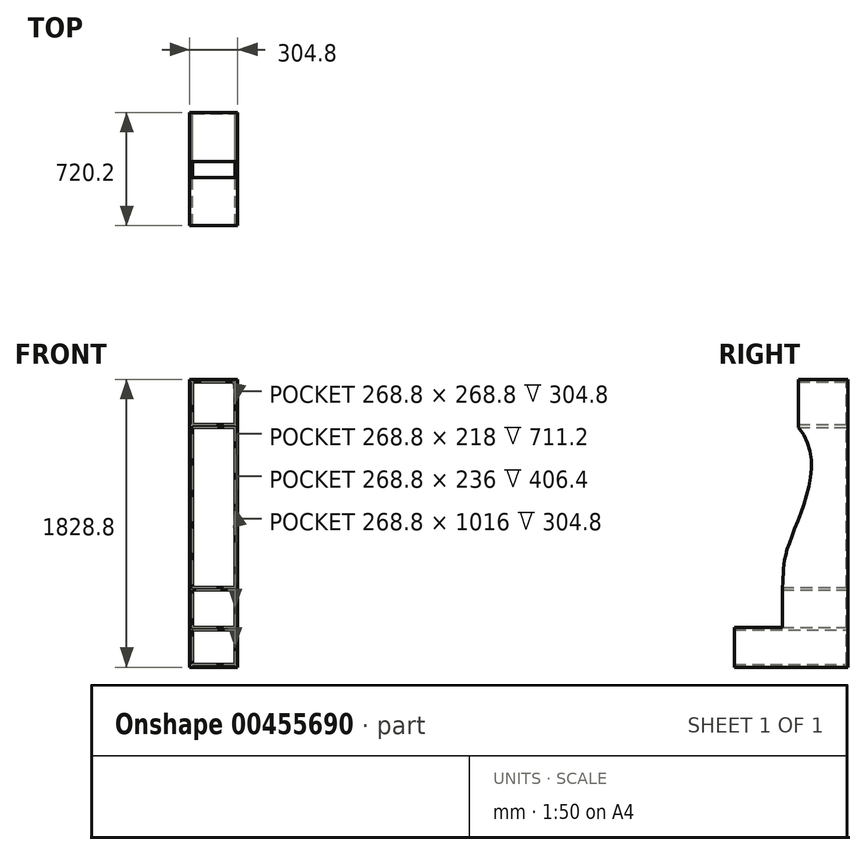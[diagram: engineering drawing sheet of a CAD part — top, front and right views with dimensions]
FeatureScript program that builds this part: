
annotation { "Feature Type Name" : "Feature", "Feature Type Description" : "" }
export const myFeature = defineFeature(function(context is Context, id is Id, definition is map)
    precondition{}
    {
        {
            var Q0;
            Q0=qCreatedBy(makeId("Front.planeOp"),FACE);
            var sketch = newSketch(context, id + "F0", { "sketchPlane" : qUnion([Q0])});
            skLineSegment(sketch, "E0.bottom", {"start": v(0, 0) * mm, "end": v(304.8, 0) * mm});
            skLineSegment(sketch, "E0.top", {"start": v(0, 1828.8) * mm, "end": v(304.8, 1828.8) * mm});
            skLineSegment(sketch, "E0.left", {"start": v(0, 0) * mm, "end": v(0, 1828.8) * mm});
            skLineSegment(sketch, "E0.right", {"start": v(304.8, 0) * mm, "end": v(304.8, 1828.8) * mm});
            skLineSegment(sketch, "E1", {"start": v(0, 254) * mm, "end": v(304.8, 254) * mm});
            skLineSegment(sketch, "E2", {"start": v(0, 508) * mm, "end": v(304.8, 508) * mm});
            skLineSegment(sketch, "E3", {"start": v(18, 1524) * mm, "end": v(286.8, 1524) * mm});
            skPoint(sketch, "E3.endSnap0", {"position": v(304.8, 914.4) * mm});
            skLineSegment(sketch, "E4.0", {"start": v(18, 236) * mm, "end": v(286.8, 236) * mm});
            skLineSegment(sketch, "E5.0", {"start": v(286.8, 18) * mm, "end": v(286.8, 236) * mm});
            skLineSegment(sketch, "E6.0", {"start": v(18, 18) * mm, "end": v(18, 236) * mm});
            skLineSegment(sketch, "E7.0", {"start": v(18, 490) * mm, "end": v(286.8, 490) * mm});
            skLineSegment(sketch, "E8.0", {"start": v(18, 18) * mm, "end": v(286.8, 18) * mm});
            skLineSegment(sketch, "E9.0", {"start": v(18, 1810.8) * mm, "end": v(286.8, 1810.8) * mm});
            skLineSegment(sketch, "E10.0", {"start": v(18, 1542) * mm, "end": v(286.8, 1542) * mm});
            skLineSegment(sketch, "E11.trimOffspring", {"start": v(286.8, 1542) * mm, "end": v(286.8, 1810.8) * mm});
            skPoint(sketch, "E12.orphan", {"position": v(304.8, 1524) * mm});
            skLineSegment(sketch, "E13.trimOffspring", {"start": v(18, 1542) * mm, "end": v(18, 1810.8) * mm});
            skLineSegment(sketch, "E14.trimOffspring", {"start": v(18, 508) * mm, "end": v(18, 1524) * mm});
            skLineSegment(sketch, "E15.trimOffspring", {"start": v(286.8, 508) * mm, "end": v(286.8, 1524) * mm});
            skLineSegment(sketch, "E16.trimOffspring", {"start": v(18, 254) * mm, "end": v(18, 490) * mm});
            skLineSegment(sketch, "E17.trimOffspring", {"start": v(286.8, 254) * mm, "end": v(286.8, 490) * mm});
            skSolve(sketch);
        }
        {
            var Q0;
            Q0=makeQuery(id+"F0.imprint","IMPRINT",FACE,{"disambiguationData":[TD([[makeQuery(id+"F0.imprint","IMPRINT",EDGE,{"derivedFrom":sQuery(id+"F0.wireOp",EDGE,"E7.0")}),1.0]])]});
            var sketch = newSketch(context, id + "F1", { "sketchPlane" : qUnion([Q0])});
            skLineSegment(sketch, "E18.0", {"start": v(18, 254) * mm, "end": v(18, 490) * mm});
            skLineSegment(sketch, "E18.1", {"start": v(18, 490) * mm, "end": v(286.8, 490) * mm});
            skLineSegment(sketch, "E18.2", {"start": v(286.8, 254) * mm, "end": v(286.8, 490) * mm});
            skLineSegment(sketch, "E18.3", {"start": v(0, 508) * mm, "end": v(304.8, 508) * mm});
            skLineSegment(sketch, "E18.4", {"start": v(0, 254) * mm, "end": v(0, 508) * mm});
            skLineSegment(sketch, "E18.5", {"start": v(304.8, 254) * mm, "end": v(304.8, 508) * mm});
            skPoint(sketch, "E19.orphan", {"position": v(0, 1828.8) * mm});
            skPoint(sketch, "E20.orphan", {"position": v(304.8, 1828.8) * mm});
            skLineSegment(sketch, "E21", {"start": v(0, 254) * mm, "end": v(18, 254) * mm});
            skLineSegment(sketch, "E22", {"start": v(286.8, 254) * mm, "end": v(304.8, 254) * mm});
            skPoint(sketch, "E23.orphan", {"position": v(304.8, 0) * mm});
            skPoint(sketch, "E24.orphan", {"position": v(0, 0) * mm});
            skSolve(sketch);
        }
        {
            var Q0;
            {var subQ4=sQuery(id+"F0.wireOp",EDGE,"E0.top");Q0=makeQuery(id+"F0.imprint","IMPRINT",FACE,{"disambiguationData":[TD([[makeQuery(id+"F0.imprint","IMPRINT",EDGE,{"derivedFrom":subQ4}),-1.0]])]});}
            var sketch = newSketch(context, id + "F2", { "sketchPlane" : qUnion([Q0])});
            skLineSegment(sketch, "E25.0", {"start": v(18, 1810.8) * mm, "end": v(286.8, 1810.8) * mm});
            skLineSegment(sketch, "E25.1", {"start": v(18, 1542) * mm, "end": v(18, 1810.8) * mm});
            skLineSegment(sketch, "E25.2", {"start": v(18, 1542) * mm, "end": v(286.8, 1542) * mm});
            skLineSegment(sketch, "E25.3", {"start": v(286.8, 1542) * mm, "end": v(286.8, 1810.8) * mm});
            skLineSegment(sketch, "E25.4", {"start": v(304.8, 1524) * mm, "end": v(304.8, 1828.8) * mm});
            skLineSegment(sketch, "E25.5", {"start": v(0, 1828.8) * mm, "end": v(304.8, 1828.8) * mm});
            skLineSegment(sketch, "E25.6", {"start": v(0, 1524) * mm, "end": v(0, 1828.8) * mm});
            skLineSegment(sketch, "E25.7", {"start": v(18, 1524) * mm, "end": v(286.8, 1524) * mm});
            skPoint(sketch, "E25.8", {"position": v(152.4, 1542) * mm});
            skLineSegment(sketch, "E26", {"start": v(18, 1524) * mm, "end": v(0, 1524) * mm});
            skLineSegment(sketch, "E27", {"start": v(286.8, 1524) * mm, "end": v(304.8, 1524) * mm});
            skPoint(sketch, "E28.orphan", {"position": v(304.8, 0) * mm});
            skPoint(sketch, "E29.orphan", {"position": v(0, 0) * mm});
            skSolve(sketch);
        }
        {
            var Q0;
            {var subQ4=sQuery(id+"F0.wireOp",EDGE,"E0.top");Q0=makeQuery(id+"F0.imprint","IMPRINT",FACE,{"disambiguationData":[TD([[makeQuery(id+"F0.imprint","IMPRINT",EDGE,{"derivedFrom":subQ4}),-1.0]])]});}
            var sketch = newSketch(context, id + "F3", { "sketchPlane" : qUnion([Q0])});
            skLineSegment(sketch, "E30.0", {"start": v(18, 508) * mm, "end": v(18, 1524) * mm});
            skLineSegment(sketch, "E30.1", {"start": v(0, 508) * mm, "end": v(0, 1524) * mm});
            skLineSegment(sketch, "E30.2", {"start": v(286.8, 508) * mm, "end": v(286.8, 1524) * mm});
            skLineSegment(sketch, "E30.3", {"start": v(304.8, 508) * mm, "end": v(304.8, 1524) * mm});
            skLineSegment(sketch, "E31", {"start": v(286.8, 508) * mm, "end": v(304.8, 508) * mm});
            skLineSegment(sketch, "E32", {"start": v(18, 508) * mm, "end": v(0, 508) * mm});
            skLineSegment(sketch, "E33", {"start": v(18, 1524) * mm, "end": v(0, 1524) * mm});
            skLineSegment(sketch, "E34", {"start": v(286.8, 1524) * mm, "end": v(304.8, 1524) * mm});
            skPoint(sketch, "E35.orphan", {"position": v(0, 1828.8) * mm});
            skPoint(sketch, "E36.orphan", {"position": v(304.8, 1828.8) * mm});
            skPoint(sketch, "E37.orphan", {"position": v(304.8, 0) * mm});
            skPoint(sketch, "E38.orphan", {"position": v(0, 0) * mm});
            skSolve(sketch);
        }
        {
            var Q0;
            {var subQ4=sQuery(id+"F0.wireOp",EDGE,"E0.bottom");Q0=makeQuery(id+"F0.imprint","IMPRINT",FACE,{"disambiguationData":[TD([[makeQuery(id+"F0.imprint","IMPRINT",EDGE,{"derivedFrom":subQ4}),1.0]])]});}
            extrude(context, id + "F4", {"entities" : qUnion([Q0]), "depth" : 711.2 * mm});
        }
        {
            var Q0;
            Q0 = qSketchRegion(id + "F1", true);
            extrude(context, id + "F5", {"entities" : qUnion([Q0]), "operationType" : NewBodyOperationType.ADD, "depth" : 406.4 * mm});
        }
        {
            var Q0;
            Q0 = qSketchRegion(id + "F2", true);
            extrude(context, id + "F6", {"entities" : qUnion([Q0]), "depth" : 304.8 * mm});
        }
        {
            var Q0;
            Q0 = qSketchRegion(id + "F3", true);
            extrude(context, id + "F7", {"entities" : qUnion([Q0]), "operationType" : NewBodyOperationType.ADD, "depth" : 406.4 * mm});
        }
        {
            var Q0;
            Q0=makeQuery(id+"F7.boolean.opBoolean","MERGE",FACE,{"derivedFrom":[makeQuery(id+"F5.boolean.opBoolean","MERGE",FACE,{"derivedFrom":[makeQuery(id+"F4.opExtrude","SWEPT_FACE",FACE,{"disambiguationData":[OSD([sQuery(id+"F0.wireOp",EDGE,"E0.right")])]}),makeQuery(id+"F5.opExtrude","SWEPT_FACE",FACE,{"disambiguationData":[OSD([sQuery(id+"F1.wireOp",EDGE,"E18.5")])]})]}),makeQuery(id+"F6.opExtrude","SWEPT_FACE",FACE,{"disambiguationData":[OSD([sQuery(id+"F2.wireOp",EDGE,"E25.4")])]}),makeQuery(id+"F7.opExtrude","SWEPT_FACE",FACE,{"disambiguationData":[OSD([sQuery(id+"F3.wireOp",EDGE,"E30.3")])]})]});
            var sketch = newSketch(context, id + "F8", { "sketchPlane" : qUnion([Q0])});
            skPoint(sketch, "E39.0", {"position": v(-406.4, 508) * mm});
            skFitSpline(sketch, "E40", {"points": [v(-406.4, 508) * mm, v(-369.4, 767.64) * mm, v(-304.8, 1524) * mm], "startDerivative": vector(77.57, 734.22) * mm, "endDerivative": vector(-918.38, 1059.14) * mm});
            skLineSegment(sketch, "E41", {"start": v(-304.8, 1524) * mm, "end": v(-406.4, 1524) * mm});
            skLineSegment(sketch, "E42", {"start": v(-406.4, 1524) * mm, "end": v(-406.4, 508) * mm});
            skSolve(sketch);
        }
        {
            var Q0;
            Q0 = qSketchRegion(id + "F8", true);
            extrude(context, id + "F9", {"entities" : qUnion([Q0]), "operationType" : NewBodyOperationType.ADD, "depth" : 25.4 * mm});
        }
        {
            var Q0;
            Q0=makeQuery(id+"F9.opExtrude","CAP_FACE",FACE,{"disambiguationData":[OSD([sQuery(id+"F8.wireOp",EDGE,"E40"),sQuery(id+"F8.wireOp",EDGE,"E41"),sQuery(id+"F8.wireOp",EDGE,"E42")])],"isStart":false});
            extrude(context, id + "F10", {"entities" : qUnion([Q0]), "operationType" : NewBodyOperationType.REMOVE, "endBound" : BoundingType.THROUGH_ALL, "oppositeDirection" : true, "depth" : 25.4 * mm});
        }
        {
            var Q0;
            Q0=makeQuery(id+"F7.boolean.opBoolean","MERGE",FACE,{"derivedFrom":[makeQuery(id+"F5.boolean.opBoolean","MERGE",FACE,{"derivedFrom":[makeQuery(id+"F4.opExtrude","CAP_FACE",FACE,{"disambiguationData":[OSD([sQuery(id+"F0.wireOp",EDGE,"E0.bottom"),sQuery(id+"F0.wireOp",EDGE,"E0.left"),sQuery(id+"F0.wireOp",EDGE,"E0.right"),sQuery(id+"F0.wireOp",EDGE,"E1"),sQuery(id+"F0.wireOp",EDGE,"E4.0"),sQuery(id+"F0.wireOp",EDGE,"E5.0"),sQuery(id+"F0.wireOp",EDGE,"E6.0"),sQuery(id+"F0.wireOp",EDGE,"E8.0")])],"isStart":true}),makeQuery(id+"F5.opExtrude","CAP_FACE",FACE,{"disambiguationData":[OSD([sQuery(id+"F1.wireOp",EDGE,"E18.0"),sQuery(id+"F1.wireOp",EDGE,"E18.1"),sQuery(id+"F1.wireOp",EDGE,"E18.2"),sQuery(id+"F1.wireOp",EDGE,"E18.3"),sQuery(id+"F1.wireOp",EDGE,"E18.4"),sQuery(id+"F1.wireOp",EDGE,"E18.5"),sQuery(id+"F1.wireOp",EDGE,"E21"),sQuery(id+"F1.wireOp",EDGE,"E22")])],"isStart":true})]}),makeQuery(id+"F6.opExtrude","CAP_FACE",FACE,{"disambiguationData":[OSD([sQuery(id+"F2.wireOp",EDGE,"E25.0"),sQuery(id+"F2.wireOp",EDGE,"E25.1"),sQuery(id+"F2.wireOp",EDGE,"E25.2"),sQuery(id+"F2.wireOp",EDGE,"E25.3"),sQuery(id+"F2.wireOp",EDGE,"E25.4"),sQuery(id+"F2.wireOp",EDGE,"E25.5"),sQuery(id+"F2.wireOp",EDGE,"E25.6"),sQuery(id+"F2.wireOp",EDGE,"E25.7"),sQuery(id+"F2.wireOp",EDGE,"E26"),sQuery(id+"F2.wireOp",EDGE,"E27")])],"isStart":true}),makeQuery(id+"F7.opExtrude","CAP_FACE",FACE,{"disambiguationData":[OSD([sQuery(id+"F3.wireOp",EDGE,"E30.0"),sQuery(id+"F3.wireOp",EDGE,"E30.1"),sQuery(id+"F3.wireOp",EDGE,"E32"),sQuery(id+"F3.wireOp",EDGE,"E33")])],"isStart":true}),makeQuery(id+"F7.opExtrude","CAP_FACE",FACE,{"disambiguationData":[OSD([sQuery(id+"F3.wireOp",EDGE,"E30.2"),sQuery(id+"F3.wireOp",EDGE,"E30.3"),sQuery(id+"F3.wireOp",EDGE,"E31"),sQuery(id+"F3.wireOp",EDGE,"E34")])],"isStart":true})]});
            var sketch = newSketch(context, id + "F11", { "sketchPlane" : qUnion([Q0])});
            skLineSegment(sketch, "E43.bottom", {"start": v(-304.8, 1828.8) * mm, "end": v(0, 1828.8) * mm});
            skLineSegment(sketch, "E43.top", {"start": v(-304.8, 0) * mm, "end": v(0, 0) * mm});
            skLineSegment(sketch, "E43.left", {"start": v(-304.8, 1828.8) * mm, "end": v(-304.8, 0) * mm});
            skLineSegment(sketch, "E43.right", {"start": v(0, 1828.8) * mm, "end": v(0, 0) * mm});
            skSolve(sketch);
        }
        {
            var Q0;
            Q0 = qSketchRegion(id + "F11", true);
            extrude(context, id + "F12", {"entities" : qUnion([Q0]), "operationType" : NewBodyOperationType.ADD, "depth" : 9 * mm});
        }
    });
